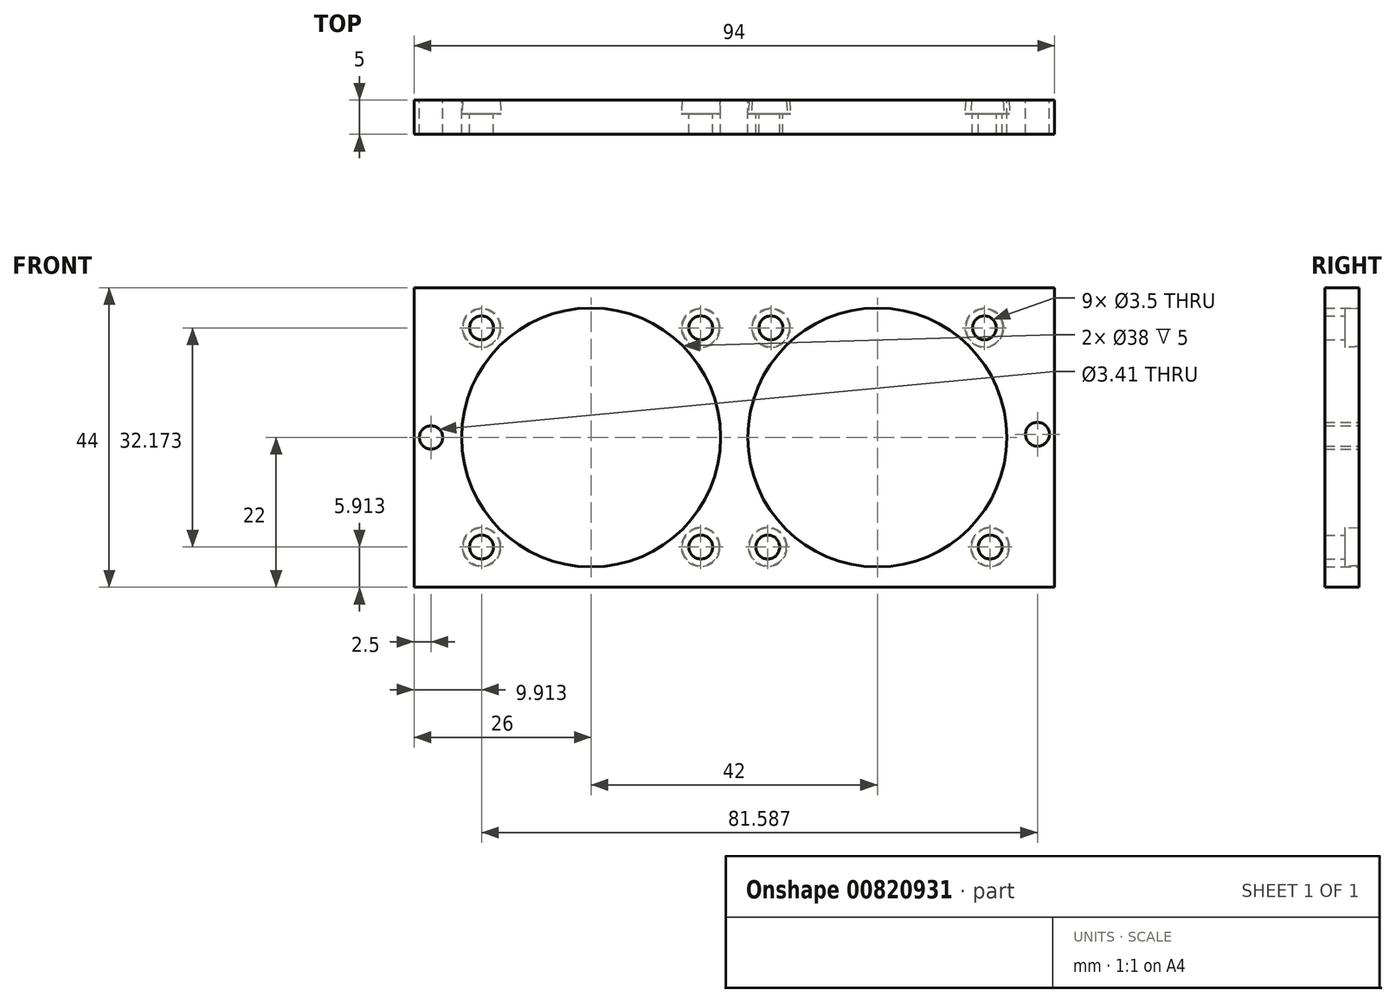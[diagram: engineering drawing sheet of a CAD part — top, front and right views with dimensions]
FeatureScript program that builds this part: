
annotation { "Feature Type Name" : "Feature", "Feature Type Description" : "" }
export const myFeature = defineFeature(function(context is Context, id is Id, definition is map)
    precondition{}
    {
        {
            var Q0;
            Q0=qCreatedBy(makeId("Front.planeOp"),FACE);
            var sketch = newSketch(context, id + "F0", { "sketchPlane" : qUnion([Q0])});
            skCircle(sketch, "E0", {"center": v(0, 0) * mm, "radius": 21 * mm, "construction": true});
            skCircle(sketch, "E1", {"center": v(-21, 0) * mm, "radius": 19 * mm});
            skCircle(sketch, "E2", {"center": v(21, 0) * mm, "radius": 19 * mm});
            skLineSegment(sketch, "E3.bottom", {"start": v(-41, 20) * mm, "end": v(-1, 20) * mm, "construction": true});
            skLineSegment(sketch, "E3.top", {"start": v(-41, -20) * mm, "end": v(-1, -20) * mm, "construction": true});
            skLineSegment(sketch, "E3.left", {"start": v(-41, 20) * mm, "end": v(-41, -20) * mm, "construction": true});
            skLineSegment(sketch, "E3.right", {"start": v(-1, 20) * mm, "end": v(-1, -20) * mm, "construction": true});
            skLineSegment(sketch, "E4.bottom", {"start": v(41, 20.47) * mm, "end": v(1, 20.47) * mm, "construction": true});
            skLineSegment(sketch, "E4.top", {"start": v(41, -20.47) * mm, "end": v(1, -20.47) * mm, "construction": true});
            skLineSegment(sketch, "E4.left", {"start": v(41, 20.47) * mm, "end": v(41, -19.53) * mm, "construction": true});
            skLineSegment(sketch, "E4.right", {"start": v(1, 20.47) * mm, "end": v(1, -20.47) * mm, "construction": true});
            skLineSegment(sketch, "E5", {"start": v(-41, 20) * mm, "end": v(-1, -20) * mm, "construction": true});
            skLineSegment(sketch, "E6", {"start": v(-1, 20) * mm, "end": v(-41, -20) * mm, "construction": true});
            skLineSegment(sketch, "E7", {"start": v(1, 20.47) * mm, "end": v(41, -19.53) * mm, "construction": true});
            skLineSegment(sketch, "E8", {"start": v(41, 20.47) * mm, "end": v(1, -20.47) * mm, "construction": true});
            skCircle(sketch, "E9", {"center": v(-21, 0) * mm, "radius": 22.75 * mm, "construction": true});
            skCircle(sketch, "E10", {"center": v(21, 0) * mm, "radius": 22.75 * mm, "construction": true});
            skCircle(sketch, "E11", {"center": v(-37.09, 16.09) * mm, "radius": 1.75 * mm});
            skCircle(sketch, "E12", {"center": v(-37.09, -16.09) * mm, "radius": 1.75 * mm});
            skCircle(sketch, "E13", {"center": v(-4.91, -16.09) * mm, "radius": 1.75 * mm});
            skCircle(sketch, "E14", {"center": v(-4.91, 16.09) * mm, "radius": 1.75 * mm});
            skCircle(sketch, "E15", {"center": v(5.38, 16.09) * mm, "radius": 1.75 * mm});
            skCircle(sketch, "E16", {"center": v(36.72, 16.09) * mm, "radius": 1.75 * mm});
            skCircle(sketch, "E17", {"center": v(37.56, -16.09) * mm, "radius": 1.75 * mm});
            skCircle(sketch, "E18", {"center": v(4.91, -16.09) * mm, "radius": 1.75 * mm});
            skLineSegment(sketch, "E19.bottom", {"start": v(47, 22) * mm, "end": v(-47, 22) * mm});
            skLineSegment(sketch, "E19.top", {"start": v(47, -22) * mm, "end": v(-47, -22) * mm});
            skLineSegment(sketch, "E19.left", {"start": v(47, 22) * mm, "end": v(47, -22) * mm});
            skLineSegment(sketch, "E19.right", {"start": v(-47, 22) * mm, "end": v(-47, -22) * mm});
            skCircle(sketch, "E20", {"center": v(-44.5, 0) * mm, "radius": 1.7 * mm});
            skPoint(sketch, "E20.centerSnap0", {"position": v(-47, 0) * mm});
            skCircle(sketch, "E21", {"center": v(44.5, 0.47) * mm, "radius": 1.75 * mm});
            skPoint(sketch, "E21.centerSnap0", {"position": v(41, 0.47) * mm});
            skCircle(sketch, "E22", {"center": v(-37.09, 16.09) * mm, "radius": 2.75 * mm});
            skCircle(sketch, "E23", {"center": v(-37.09, -16.09) * mm, "radius": 2.75 * mm});
            skCircle(sketch, "E24", {"center": v(-4.91, -16.09) * mm, "radius": 2.75 * mm});
            skCircle(sketch, "E25", {"center": v(-4.91, 16.09) * mm, "radius": 2.75 * mm});
            skCircle(sketch, "E26", {"center": v(5.38, 16.09) * mm, "radius": 2.75 * mm});
            skCircle(sketch, "E27", {"center": v(36.72, 16.09) * mm, "radius": 2.75 * mm});
            skCircle(sketch, "E28", {"center": v(37.56, -16.09) * mm, "radius": 2.75 * mm});
            skCircle(sketch, "E29", {"center": v(4.91, -16.09) * mm, "radius": 2.75 * mm});
            skSolve(sketch);
        }
        {
            var Q0;
            Q0=makeQuery(id+"F0.imprint","IMPRINT",FACE,{"disambiguationData":[TD([[makeQuery(id+"F0.imprint","IMPRINT",EDGE,{"derivedFrom":sQuery(id+"F0.wireOp",EDGE,"E1")}),-1.0]])]});
            var Q1;
            Q1=makeQuery(id+"F0.imprint","IMPRINT",FACE,{"disambiguationData":[TD([[makeQuery(id+"F0.imprint","IMPRINT",EDGE,{"derivedFrom":sQuery(id+"F0.wireOp",EDGE,"E11")}),-1.0]])]});
            var Q2;
            Q2=makeQuery(id+"F0.imprint","IMPRINT",FACE,{"disambiguationData":[TD([[makeQuery(id+"F0.imprint","IMPRINT",EDGE,{"derivedFrom":sQuery(id+"F0.wireOp",EDGE,"E14")}),-1.0]])]});
            var Q3;
            Q3=makeQuery(id+"F0.imprint","IMPRINT",FACE,{"disambiguationData":[TD([[makeQuery(id+"F0.imprint","IMPRINT",EDGE,{"derivedFrom":sQuery(id+"F0.wireOp",EDGE,"E12")}),-1.0]])]});
            var Q4;
            Q4=makeQuery(id+"F0.imprint","IMPRINT",FACE,{"disambiguationData":[TD([[makeQuery(id+"F0.imprint","IMPRINT",EDGE,{"derivedFrom":sQuery(id+"F0.wireOp",EDGE,"E13")}),-1.0]])]});
            var Q5;
            Q5=makeQuery(id+"F0.imprint","IMPRINT",FACE,{"disambiguationData":[TD([[makeQuery(id+"F0.imprint","IMPRINT",EDGE,{"derivedFrom":sQuery(id+"F0.wireOp",EDGE,"E15")}),-1.0]])]});
            var Q6;
            Q6=makeQuery(id+"F0.imprint","IMPRINT",FACE,{"disambiguationData":[TD([[makeQuery(id+"F0.imprint","IMPRINT",EDGE,{"derivedFrom":sQuery(id+"F0.wireOp",EDGE,"E16")}),-1.0]])]});
            var Q7;
            Q7=makeQuery(id+"F0.imprint","IMPRINT",FACE,{"disambiguationData":[TD([[makeQuery(id+"F0.imprint","IMPRINT",EDGE,{"derivedFrom":sQuery(id+"F0.wireOp",EDGE,"E17")}),-1.0]])]});
            var Q8;
            Q8=makeQuery(id+"F0.imprint","IMPRINT",FACE,{"disambiguationData":[TD([[makeQuery(id+"F0.imprint","IMPRINT",EDGE,{"derivedFrom":sQuery(id+"F0.wireOp",EDGE,"E18")}),-1.0]])]});
            extrude(context, id + "F1", {"entities" : qUnion([Q0, Q1, Q2, Q3, Q4, Q5, Q6, Q7, Q8]), "depth" : 5 * mm, "offsetDistance" : 25 * mm});
        }
        {
            var Q0;
            Q0=makeQuery(id+"F0.imprint","IMPRINT",FACE,{"disambiguationData":[TD([[makeQuery(id+"F0.imprint","IMPRINT",EDGE,{"derivedFrom":sQuery(id+"F0.wireOp",EDGE,"E11")}),-1.0]])]});
            var Q1;
            Q1=makeQuery(id+"F0.imprint","IMPRINT",FACE,{"disambiguationData":[TD([[makeQuery(id+"F0.imprint","IMPRINT",EDGE,{"derivedFrom":sQuery(id+"F0.wireOp",EDGE,"E12")}),-1.0]])]});
            var Q2;
            Q2=makeQuery(id+"F0.imprint","IMPRINT",FACE,{"disambiguationData":[TD([[makeQuery(id+"F0.imprint","IMPRINT",EDGE,{"derivedFrom":sQuery(id+"F0.wireOp",EDGE,"E13")}),-1.0]])]});
            var Q3;
            Q3=makeQuery(id+"F0.imprint","IMPRINT",FACE,{"disambiguationData":[TD([[makeQuery(id+"F0.imprint","IMPRINT",EDGE,{"derivedFrom":sQuery(id+"F0.wireOp",EDGE,"E18")}),-1.0]])]});
            var Q4;
            Q4=makeQuery(id+"F0.imprint","IMPRINT",FACE,{"disambiguationData":[TD([[makeQuery(id+"F0.imprint","IMPRINT",EDGE,{"derivedFrom":sQuery(id+"F0.wireOp",EDGE,"E17")}),-1.0]])]});
            var Q5;
            Q5=makeQuery(id+"F0.imprint","IMPRINT",FACE,{"disambiguationData":[TD([[makeQuery(id+"F0.imprint","IMPRINT",EDGE,{"derivedFrom":sQuery(id+"F0.wireOp",EDGE,"E16")}),-1.0]])]});
            var Q6;
            Q6=makeQuery(id+"F0.imprint","IMPRINT",FACE,{"disambiguationData":[TD([[makeQuery(id+"F0.imprint","IMPRINT",EDGE,{"derivedFrom":sQuery(id+"F0.wireOp",EDGE,"E15")}),-1.0]])]});
            var Q7;
            Q7=makeQuery(id+"F0.imprint","IMPRINT",FACE,{"disambiguationData":[TD([[makeQuery(id+"F0.imprint","IMPRINT",EDGE,{"derivedFrom":sQuery(id+"F0.wireOp",EDGE,"E14")}),-1.0]])]});
            var Q8;
            Q8=sQuery(id+"F0.wireOp",EDGE,"E22");
            var Q9;
            Q9=sQuery(id+"F0.wireOp",EDGE,"E23");
            var Q10;
            Q10=sQuery(id+"F0.wireOp",EDGE,"E25");
            var Q11;
            Q11=sQuery(id+"F0.wireOp",EDGE,"E24");
            var Q12;
            Q12=sQuery(id+"F0.wireOp",EDGE,"E29");
            var Q13;
            Q13=sQuery(id+"F0.wireOp",EDGE,"E26");
            var Q14;
            Q14=sQuery(id+"F0.wireOp",EDGE,"E27");
            var Q15;
            Q15=sQuery(id+"F0.wireOp",EDGE,"E28");
            extrude(context, id + "F2", {"entities" : qUnion([Q0, Q1, Q2, Q3, Q4, Q5, Q6, Q7]), "operationType" : NewBodyOperationType.REMOVE, "surfaceOperationType" : NewSurfaceOperationType.ADD, "surfaceEntities" : qUnion([Q8, Q9, Q10, Q11, Q12, Q13, Q14, Q15]), "depth" : 2 * mm, "offsetDistance" : 25 * mm, "hasDraft" : true, "draftAngle" : 3 * degree});
        }
    });
